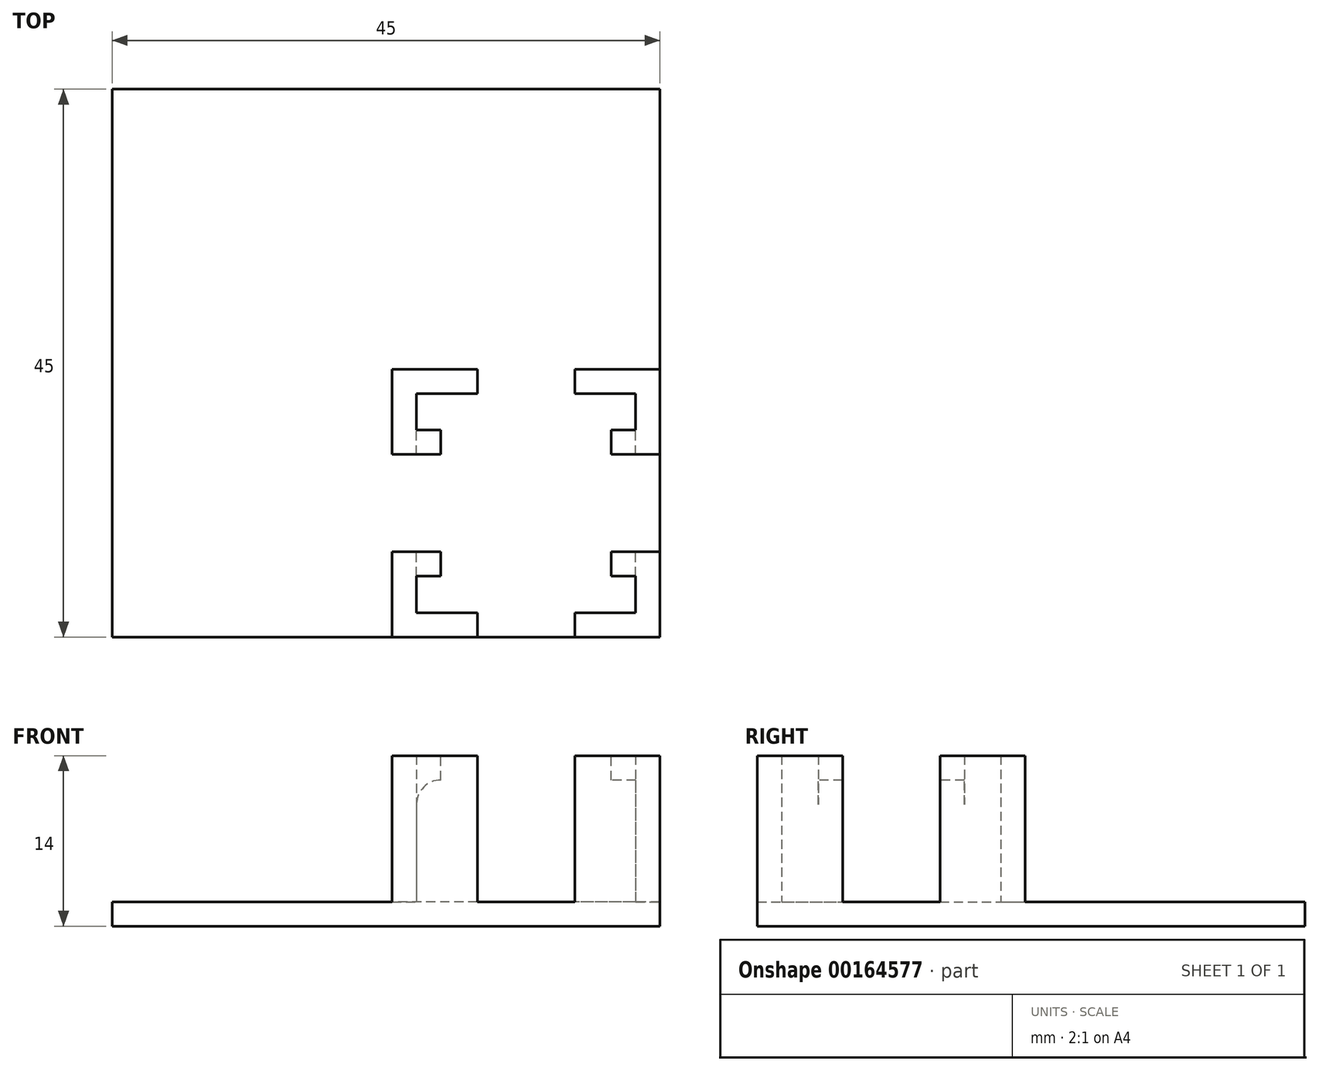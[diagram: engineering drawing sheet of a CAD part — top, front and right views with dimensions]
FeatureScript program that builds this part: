
annotation { "Feature Type Name" : "Feature", "Feature Type Description" : "" }
export const myFeature = defineFeature(function(context is Context, id is Id, definition is map)
    precondition{}
    {
        {
            var Q0;
            Q0=qCreatedBy(makeId("Top.planeOp"),FACE);
            var sketch = newSketch(context, id + "F0", { "sketchPlane" : qUnion([Q0])});
            skLineSegment(sketch, "E0.bottom", {"start": v(0, 0) * mm, "end": v(45, 0) * mm});
            skLineSegment(sketch, "E0.top", {"start": v(0, -45) * mm, "end": v(45, -45) * mm});
            skLineSegment(sketch, "E0.left", {"start": v(0, 0) * mm, "end": v(0, -45) * mm});
            skLineSegment(sketch, "E0.right", {"start": v(45, 0) * mm, "end": v(45, -45) * mm});
            skSolve(sketch);
        }
        {
            var Q0;
            Q0 = qSketchRegion(id + "F0", true);
            extrude(context, id + "F1", {"entities" : qUnion([Q0]), "depth" : 2 * mm});
        }
        {
            var Q0;
            Q0=makeQuery(id+"F1.opExtrude","CAP_FACE",FACE,{"disambiguationData":[OSD([sQuery(id+"F0.wireOp",EDGE,"E0.bottom"),sQuery(id+"F0.wireOp",EDGE,"E0.top"),sQuery(id+"F0.wireOp",EDGE,"E0.left"),sQuery(id+"F0.wireOp",EDGE,"E0.right")])],"isStart":false});
            var sketch = newSketch(context, id + "F2", { "sketchPlane" : qUnion([Q0])});
            skLineSegment(sketch, "E1.bottom", {"start": v(45, -45) * mm, "end": v(23, -45) * mm});
            skLineSegment(sketch, "E1.top", {"start": v(45, -23) * mm, "end": v(23, -23) * mm});
            skLineSegment(sketch, "E1.left", {"start": v(45, -45) * mm, "end": v(45, -23) * mm});
            skLineSegment(sketch, "E1.right", {"start": v(23, -45) * mm, "end": v(23, -23) * mm});
            skLineSegment(sketch, "E2.0", {"start": v(43, -25) * mm, "end": v(25, -25) * mm});
            skLineSegment(sketch, "E2.1", {"start": v(43, -43) * mm, "end": v(43, -25) * mm});
            skLineSegment(sketch, "E2.2", {"start": v(43, -43) * mm, "end": v(25, -43) * mm});
            skLineSegment(sketch, "E2.3", {"start": v(25, -43) * mm, "end": v(25, -25) * mm});
            skSolve(sketch);
        }
        {
            var Q0;
            Q0 = qSketchRegion(id + "F2", true);
            extrude(context, id + "F3", {"entities" : qUnion([Q0]), "operationType" : NewBodyOperationType.ADD, "depth" : 10 * mm});
        }
        {
            var Q0;
            Q0=makeQuery(id+"F3.opExtrude","CAP_FACE",FACE,{"disambiguationData":[OSD([sQuery(id+"F2.wireOp",EDGE,"E1.bottom"),sQuery(id+"F2.wireOp",EDGE,"E1.top"),sQuery(id+"F2.wireOp",EDGE,"E1.left"),sQuery(id+"F2.wireOp",EDGE,"E1.right"),sQuery(id+"F2.wireOp",EDGE,"E2.0"),sQuery(id+"F2.wireOp",EDGE,"E2.1"),sQuery(id+"F2.wireOp",EDGE,"E2.2"),sQuery(id+"F2.wireOp",EDGE,"E2.3")])],"isStart":false});
            var sketch = newSketch(context, id + "F4", { "sketchPlane" : qUnion([Q0])});
            skLineSegment(sketch, "E3.0", {"start": v(45, -23) * mm, "end": v(23, -23) * mm});
            skLineSegment(sketch, "E3.1", {"start": v(23, -45) * mm, "end": v(23, -23) * mm});
            skLineSegment(sketch, "E3.2", {"start": v(25, -43) * mm, "end": v(25, -25) * mm});
            skLineSegment(sketch, "E3.3", {"start": v(23, -45) * mm, "end": v(45, -45) * mm});
            skLineSegment(sketch, "E3.4", {"start": v(43, -43) * mm, "end": v(25, -43) * mm});
            skLineSegment(sketch, "E3.5", {"start": v(43, -43) * mm, "end": v(43, -25) * mm});
            skLineSegment(sketch, "E3.6", {"start": v(45, -23) * mm, "end": v(45, -45) * mm});
            skLineSegment(sketch, "E3.7", {"start": v(43, -25) * mm, "end": v(25, -25) * mm});
            skLineSegment(sketch, "E4.bottom", {"start": v(27, -25) * mm, "end": v(41, -25) * mm});
            skLineSegment(sketch, "E4.top", {"start": v(27, -27) * mm, "end": v(41, -27) * mm});
            skLineSegment(sketch, "E4.left", {"start": v(27, -25) * mm, "end": v(27, -27) * mm});
            skLineSegment(sketch, "E4.right", {"start": v(41, -25) * mm, "end": v(41, -27) * mm});
            skLineSegment(sketch, "E5.bottom", {"start": v(28, -43) * mm, "end": v(41, -43) * mm});
            skLineSegment(sketch, "E5.top", {"start": v(28, -41) * mm, "end": v(41, -41) * mm});
            skLineSegment(sketch, "E5.left", {"start": v(28, -43) * mm, "end": v(28, -41) * mm});
            skLineSegment(sketch, "E5.right", {"start": v(41, -43) * mm, "end": v(41, -41) * mm});
            skLineSegment(sketch, "E6.bottom", {"start": v(25, -28) * mm, "end": v(27, -28) * mm});
            skLineSegment(sketch, "E6.top", {"start": v(25, -40) * mm, "end": v(27, -40) * mm});
            skLineSegment(sketch, "E6.left", {"start": v(25, -28) * mm, "end": v(25, -40) * mm});
            skLineSegment(sketch, "E6.right", {"start": v(27, -28) * mm, "end": v(27, -40) * mm});
            skLineSegment(sketch, "E7.bottom", {"start": v(43, -28) * mm, "end": v(41, -28) * mm});
            skLineSegment(sketch, "E7.top", {"start": v(43, -40) * mm, "end": v(41, -40) * mm});
            skLineSegment(sketch, "E7.left", {"start": v(43, -28) * mm, "end": v(43, -40) * mm});
            skLineSegment(sketch, "E7.right", {"start": v(41, -28) * mm, "end": v(41, -40) * mm});
            skSolve(sketch);
        }
        {
            var Q0;
            Q0 = qSketchRegion(id + "F4", true);
            var Q1;
            Q1=makeQuery(id+"F4.imprint","IMPRINT",FACE,{"disambiguationData":[TD([[makeQuery(id+"F4.imprint","IMPRINT",EDGE,{"derivedFrom":sQuery(id+"F4.wireOp",EDGE,"E6.bottom")}),-1.0]])]});
            var Q2;
            Q2=makeQuery(id+"F4.imprint","IMPRINT",FACE,{"disambiguationData":[TD([[makeQuery(id+"F4.imprint","IMPRINT",EDGE,{"derivedFrom":sQuery(id+"F4.wireOp",EDGE,"E4.bottom")}),1.0]])]});
            var Q3;
            Q3=makeQuery(id+"F4.imprint","IMPRINT",FACE,{"disambiguationData":[TD([[makeQuery(id+"F4.imprint","IMPRINT",EDGE,{"derivedFrom":sQuery(id+"F4.wireOp",EDGE,"E7.bottom")}),1.0]])]});
            var Q4;
            Q4=makeQuery(id+"F4.imprint","IMPRINT",FACE,{"disambiguationData":[TD([[makeQuery(id+"F4.imprint","IMPRINT",EDGE,{"derivedFrom":sQuery(id+"F4.wireOp",EDGE,"E5.bottom")}),-1.0]])]});
            extrude(context, id + "F5", {"entities" : qUnion([Q0, Q1, Q2, Q3, Q4]), "operationType" : NewBodyOperationType.ADD, "depth" : 2 * mm});
        }
        {
            var Q0;
            Q0=makeQuery(id+"F3.opExtrude","CAP_EDGE",EDGE,{"disambiguationData":[OSD([sQuery(id+"F2.wireOp",EDGE,"E2.3")])],"isStart":false});
            var Q1;
            Q1=makeQuery(id+"F3.opExtrude","CAP_EDGE",EDGE,{"disambiguationData":[OSD([sQuery(id+"F2.wireOp",EDGE,"E2.1")])],"isStart":false});
            var Q2;
            Q2=makeQuery(id+"F3.opExtrude","CAP_EDGE",EDGE,{"disambiguationData":[OSD([sQuery(id+"F2.wireOp",EDGE,"E2.0")])],"isStart":false});
            var Q3;
            Q3=makeQuery(id+"F3.opExtrude","CAP_EDGE",EDGE,{"disambiguationData":[OSD([sQuery(id+"F2.wireOp",EDGE,"E2.2")])],"isStart":false});
            fillet(context, id + "F6", {"entities" : qUnion([Q0, Q1, Q2, Q3]), "radius" : 2 * mm, "tangentPropagation" : true, "allowEdgeOverflow" : false});
        }
        {
            var Q0;
            Q0=makeQuery(id+"F5.opExtrude","CAP_FACE",FACE,{"disambiguationData":[OSD([sQuery(id+"F4.wireOp",EDGE,"E3.0"),sQuery(id+"F4.wireOp",EDGE,"E3.1"),sQuery(id+"F4.wireOp",EDGE,"E3.2"),sQuery(id+"F4.wireOp",EDGE,"E3.3"),sQuery(id+"F4.wireOp",EDGE,"E3.4"),sQuery(id+"F4.wireOp",EDGE,"E3.5"),sQuery(id+"F4.wireOp",EDGE,"E3.6"),sQuery(id+"F4.wireOp",EDGE,"E3.7"),sQuery(id+"F4.wireOp",EDGE,"E4.top"),sQuery(id+"F4.wireOp",EDGE,"E4.left"),sQuery(id+"F4.wireOp",EDGE,"E4.right"),sQuery(id+"F4.wireOp",EDGE,"E5.top"),sQuery(id+"F4.wireOp",EDGE,"E5.left"),sQuery(id+"F4.wireOp",EDGE,"E5.right"),sQuery(id+"F4.wireOp",EDGE,"E6.bottom"),sQuery(id+"F4.wireOp",EDGE,"E6.top"),sQuery(id+"F4.wireOp",EDGE,"E6.right"),sQuery(id+"F4.wireOp",EDGE,"E7.bottom"),sQuery(id+"F4.wireOp",EDGE,"E7.top"),sQuery(id+"F4.wireOp",EDGE,"E7.right")])],"isStart":false});
            var sketch = newSketch(context, id + "F7", { "sketchPlane" : qUnion([Q0])});
            skPoint(sketch, "E8.0", {"position": v(34, -23) * mm});
            skPoint(sketch, "E8.1", {"position": v(23, -34) * mm});
            skLineSegment(sketch, "E9", {"start": v(34, -23) * mm, "end": v(34, -47.55) * mm, "construction": true});
            skLineSegment(sketch, "E10", {"start": v(23, -34) * mm, "end": v(23, -34) * mm});
            skPoint(sketch, "E10.endSnap0", {"position": v(45, -34) * mm});
            skLineSegment(sketch, "E11.bottom", {"start": v(49, -38) * mm, "end": v(19, -38) * mm});
            skLineSegment(sketch, "E11.top", {"start": v(49, -30) * mm, "end": v(19, -30) * mm});
            skLineSegment(sketch, "E11.left", {"start": v(49, -38) * mm, "end": v(49, -30) * mm});
            skLineSegment(sketch, "E11.right", {"start": v(19, -38) * mm, "end": v(19, -30) * mm});
            skPoint(sketch, "E11.middle", {"position": v(34, -34) * mm});
            skLineSegment(sketch, "E12.bottom", {"start": v(38, -19) * mm, "end": v(30, -19) * mm});
            skLineSegment(sketch, "E12.top", {"start": v(38, -49) * mm, "end": v(30, -49) * mm});
            skLineSegment(sketch, "E12.left", {"start": v(38, -19) * mm, "end": v(38, -49) * mm});
            skLineSegment(sketch, "E12.right", {"start": v(30, -19) * mm, "end": v(30, -49) * mm});
            skLineSegment(sketch, "E13", {"start": v(23, -34) * mm, "end": v(45, -34) * mm, "construction": true});
            skSolve(sketch);
        }
        {
            var Q0;
            Q0 = qSketchRegion(id + "F7", true);
            var Q1;
            {var subQ0=sQuery(id+"F0.wireOp",EDGE,"E0.right");var subQ1=sQuery(id+"F0.wireOp",EDGE,"E0.left");var subQ2=sQuery(id+"F0.wireOp",EDGE,"E0.top");var subQ3=sQuery(id+"F0.wireOp",EDGE,"E0.bottom");Q1=makeQuery(id+"F3.boolean.opBoolean","SPLIT",FACE,{"disambiguationData":[TD([makeQuery(id+"F1.opExtrude","SWEPT_FACE",FACE,{"disambiguationData":[OSD([subQ3])]})])],"derivedFrom":makeQuery(id+"F1.opExtrude","CAP_FACE",FACE,{"disambiguationData":[OSD([subQ3,subQ2,subQ1,subQ0])],"isStart":false})});}
            extrude(context, id + "F8", {"entities" : qUnion([Q0]), "operationType" : NewBodyOperationType.REMOVE, "endBound" : BoundingType.UP_TO_SURFACE, "oppositeDirection" : true, "endBoundEntityFace" : qUnion([Q1]), "depth" : 25 * mm});
        }
    });
